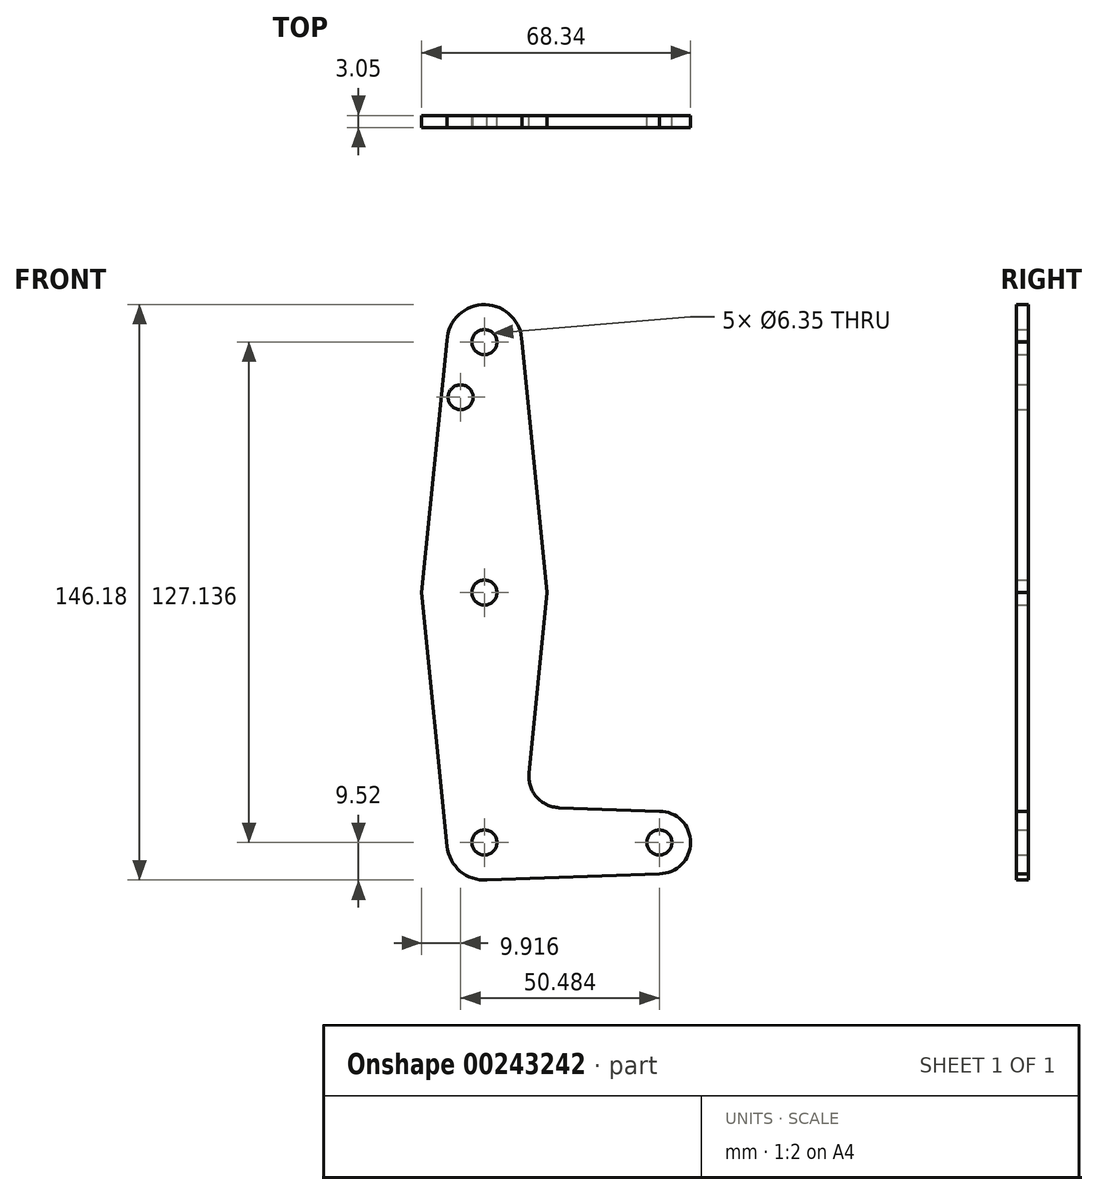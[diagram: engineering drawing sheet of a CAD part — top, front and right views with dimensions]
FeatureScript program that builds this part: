
annotation { "Feature Type Name" : "Feature", "Feature Type Description" : "" }
export const myFeature = defineFeature(function(context is Context, id is Id, definition is map)
    precondition{}
    {
        {
            var Q0;
            Q0=qCreatedBy(makeId("Front.planeOp"),FACE);
            var sketch = newSketch(context, id + "F0", { "sketchPlane" : qUnion([Q0])});
            skLineSegment(sketch, "E0", {"start": v(-44.45, 63.64) * mm, "end": v(-44.45, 60.46) * mm});
            skCircle(sketch, "E1", {"center": v(-44.45, 63.64) * mm, "radius": 9.53 * mm});
            skCircle(sketch, "E2", {"center": v(-44.45, 0) * mm, "radius": 15.88 * mm});
            skCircle(sketch, "E3", {"center": v(-44.45, -63.5) * mm, "radius": 9.53 * mm});
            skCircle(sketch, "E4", {"center": v(0, -63.5) * mm, "radius": 7.94 * mm});
            skLineSegment(sketch, "E5", {"start": v(-44.45, -63.5) * mm, "end": v(0, -63.5) * mm});
            skLineSegment(sketch, "E6", {"start": v(-53.96, 64.08) * mm, "end": v(-60.4, 0) * mm});
            skLineSegment(sketch, "E7", {"start": v(-34.93, 63.64) * mm, "end": v(-28.5, 0) * mm});
            skLineSegment(sketch, "E8", {"start": v(-60.4, 0) * mm, "end": v(-53.93, -64.45) * mm});
            skLineSegment(sketch, "E9", {"start": v(-28.5, 0) * mm, "end": v(-33.1, -45.91) * mm});
            skLineSegment(sketch, "E10", {"start": v(-25.48, -54.65) * mm, "end": v(0, -55.56) * mm});
            skLineSegment(sketch, "E11", {"start": v(-44.45, -73.02) * mm, "end": v(0, -71.44) * mm});
            skCircle(sketch, "E12", {"center": v(-44.45, 63.64) * mm, "radius": 3.18 * mm});
            skCircle(sketch, "E13", {"center": v(-44.45, 0) * mm, "radius": 3.18 * mm});
            skCircle(sketch, "E14", {"center": v(-44.45, -63.5) * mm, "radius": 3.18 * mm});
            skCircle(sketch, "E15", {"center": v(0, -63.5) * mm, "radius": 3.18 * mm});
            skArc(sketch, "E16.filletArc", {"start": v(-33.1, -45.91) * mm, "mid": v(-31.19, -51.93) * mm, "end": v(-25.48, -54.65) * mm});
            skLineSegment(sketch, "E17.trimOffspring", {"start": v(-44.45, 3.18) * mm, "end": v(-44.45, -3.18) * mm});
            skLineSegment(sketch, "E18.trimOffspring", {"start": v(-44.45, -60.33) * mm, "end": v(-44.45, -63.5) * mm});
            skLineSegment(sketch, "E19", {"start": v(-44.45, 63.64) * mm, "end": v(-44.45, 0) * mm});
            skCircle(sketch, "E20", {"center": v(-50.48, 49.62) * mm, "radius": 3.18 * mm});
            skSolve(sketch);
        }
        {
            var Q0;
            Q0 = qSketchRegion(id + "F0", true);
            extrude(context, id + "F1", {"entities" : qUnion([Q0]), "depth" : 3.05 * mm});
        }
    });
